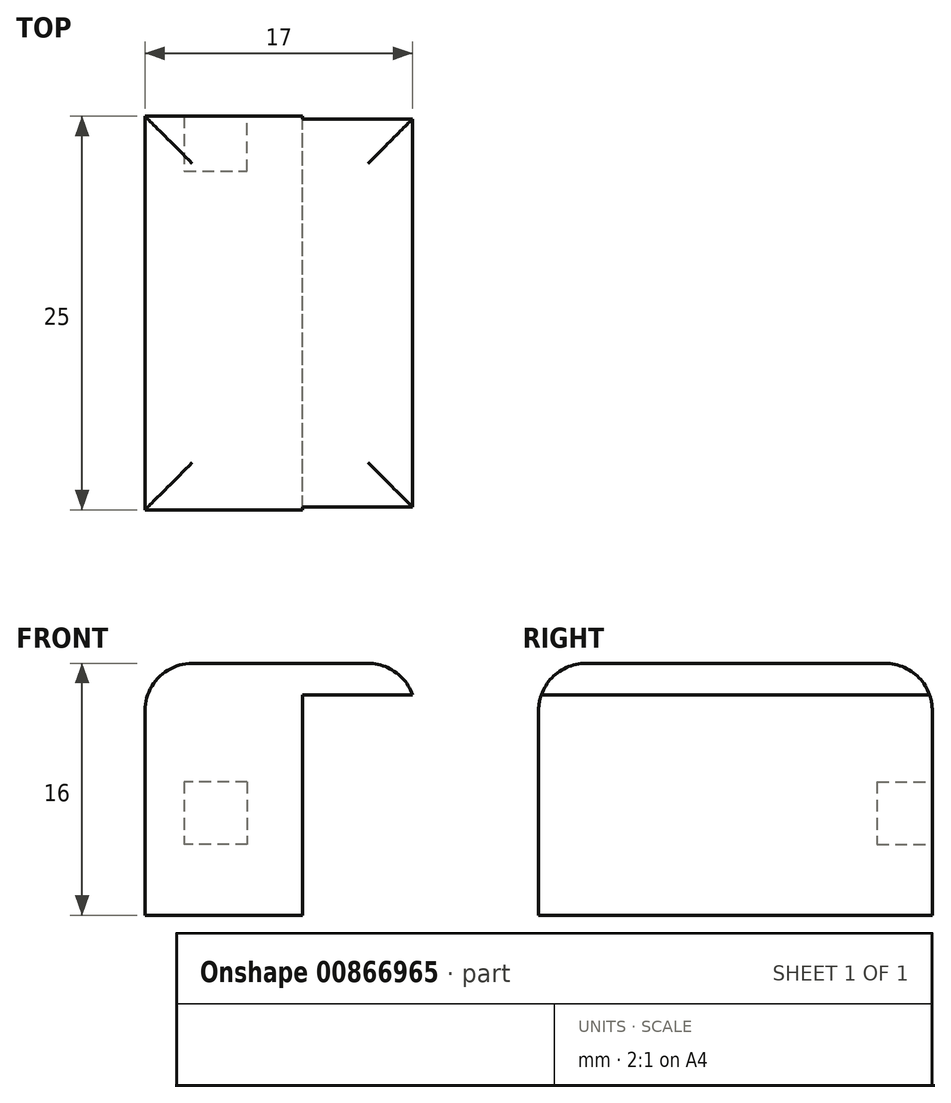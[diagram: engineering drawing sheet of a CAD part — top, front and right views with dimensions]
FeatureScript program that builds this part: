
annotation { "Feature Type Name" : "Feature", "Feature Type Description" : "" }
export const myFeature = defineFeature(function(context is Context, id is Id, definition is map)
    precondition{}
    {
        {
            var Q0;
            Q0=qCreatedBy(makeId("Top.planeOp"),FACE);
            var sketch = newSketch(context, id + "F0", { "sketchPlane" : qUnion([Q0])});
            skLineSegment(sketch, "E0.bottom", {"start": v(3.5, -17.35) * mm, "end": v(-6.5, -17.35) * mm});
            skLineSegment(sketch, "E0.top", {"start": v(3.5, 7.65) * mm, "end": v(-6.5, 7.65) * mm});
            skLineSegment(sketch, "E0.left", {"start": v(3.5, -17.35) * mm, "end": v(3.5, 7.65) * mm});
            skLineSegment(sketch, "E0.right", {"start": v(-6.5, -17.35) * mm, "end": v(-6.5, 7.65) * mm});
            skPoint(sketch, "E0.middle", {"position": v(-1.5, -4.85) * mm});
            skLineSegment(sketch, "E1", {"start": v(3.5, 7.65) * mm, "end": v(10.5, 7.65) * mm});
            skLineSegment(sketch, "E2", {"start": v(3.5, -17.35) * mm, "end": v(10.5, -17.35) * mm});
            skLineSegment(sketch, "E3", {"start": v(10.5, -17.35) * mm, "end": v(10.5, 7.65) * mm});
            skLineSegment(sketch, "E4", {"start": v(-6.5, 11.15) * mm, "end": v(-4, 11.15) * mm});
            skLineSegment(sketch, "E5", {"start": v(-6.5, 13.23) * mm, "end": v(0, 13.23) * mm});
            skLineSegment(sketch, "E6", {"start": v(-4, 7.65) * mm, "end": v(-4, 4.15) * mm});
            skLineSegment(sketch, "E7", {"start": v(-4, 4.15) * mm, "end": v(0, 4.15) * mm});
            skLineSegment(sketch, "E8", {"start": v(0, 4.15) * mm, "end": v(0, 7.65) * mm});
            skSolve(sketch);
        }
        {
            var Q0;
            Q0=makeQuery(id+"F0.imprint","IMPRINT",FACE,{"disambiguationData":[TD([[makeQuery(id+"F0.imprint","IMPRINT",EDGE,{"derivedFrom":sQuery(id+"F0.wireOp",EDGE,"E0.bottom")}),-1.0]])]});
            var Q1;
            {var subQ0=sQuery(id+"F0.wireOp",EDGE,"E6");Q1=makeQuery(id+"F0.imprint","IMPRINT",FACE,{"disambiguationData":[TD([[makeQuery(id+"F0.imprint","IMPRINT",EDGE,{"derivedFrom":subQ0}),1.0]])]});}
            extrude(context, id + "F1", {"entities" : qUnion([Q0, Q1]), "depth" : 16 * mm, "offsetDistance" : 25 * mm});
        }
        {
            var Q0;
            Q0=makeQuery(id+"F0.imprint","IMPRINT",FACE,{"disambiguationData":[TD([[makeQuery(id+"F0.imprint","IMPRINT",EDGE,{"derivedFrom":sQuery(id+"F0.wireOp",EDGE,"E0.left")}),-1.0]])]});
            extrude(context, id + "F2", {"entities" : qUnion([Q0]), "operationType" : NewBodyOperationType.ADD, "depth" : 16 * mm, "offsetDistance" : 25 * mm, "hasSecondDirection" : true, "secondDirectionOppositeDirection" : false, "secondDirectionDepth" : 14 * mm});
        }
        {
            var Q0;
            {var subQ0=sQuery(id+"F0.wireOp",EDGE,"E6");Q0=makeQuery(id+"F0.imprint","IMPRINT",FACE,{"disambiguationData":[TD([[makeQuery(id+"F0.imprint","IMPRINT",EDGE,{"derivedFrom":subQ0}),1.0]])]});}
            extrude(context, id + "F3", {"entities" : qUnion([Q0]), "operationType" : NewBodyOperationType.REMOVE, "depth" : ((5 - 0.5) + 4) * mm, "offsetDistance" : 25 * mm, "hasSecondDirection" : true, "secondDirectionOppositeDirection" : false, "secondDirectionDepth" : (5 - 0.5) * mm});
        }
        {
            var Q0;
            {var subQ0=sQuery(id+"F0.wireOp",EDGE,"E0.left");Q0=makeQuery(id+"F2.boolean.opBoolean","MERGE",FACE,{"derivedFrom":[makeQuery(id+"F1.opExtrude","CAP_FACE",FACE,{"disambiguationData":[OSD([sQuery(id+"F0.wireOp",EDGE,"E0.bottom"),sQuery(id+"F0.wireOp",EDGE,"E0.top"),subQ0,sQuery(id+"F0.wireOp",EDGE,"E0.right")])],"isStart":false}),makeQuery(id+"F2.opExtrude","CAP_FACE",FACE,{"disambiguationData":[OSD([subQ0,sQuery(id+"F0.wireOp",EDGE,"E1"),sQuery(id+"F0.wireOp",EDGE,"E2"),sQuery(id+"F0.wireOp",EDGE,"E3")])],"isStart":false})]});}
            fillet(context, id + "F4", {"entities" : qUnion([Q0]), "radius" : 3 * mm, "tangentPropagation" : true, "allowEdgeOverflow" : false});
        }
    });
